# Revit family: Hager-IC-IP30-syst-PL-en
name_source: partatom
category: Electrical Equipment
units: mm (PartAtom-declared; Revit-internal decimal feet)

## family parameters
Cut with Voids When Loaded = No
Host = Face
Panel Configuration = Two Columns, Circuits Across
Part Type = Panelboard
Room Calculation Point = No
Round Connector Dimension = Use Diameter
Shared = No

## types (14) — shared parameters
EF000007 - Colour = EV000202 - White
EF000116 - RAL-number = 9010
EF000118 - With mounting plate = No
EF001062 - EMC-version = No
EF001088 - Extension possible = Yes
EF001131 - Internal depth = 72 mm  [stored 0.23622 ft]
EF001134 - DIN-rail = Yes
EF001596 - Material housing = EV000139 - Plastic
EF004462 - Type of closure = EV000154 - Other
EF005474 - Degree of protection (IP) = EV006410 - IP30
EF006244 - Transparent cover/door = No
EF006306 - With lock = No
EF009212 - Cover model = EV000116 - Closed
EF015941 - Signal passing door = Yes
HG000001 - Number of columns = 1
HG000002 - With door or cover = No
HG000003 - Range = IC
HG000005 - Thickness = 3 mm  [stored 0.00984252 ft]
HG000009 - Double swing door = No
HG000010 - Asymmetric doors = No
HG000011 - Empty rows from bottom = No
HG000017 - Distance between poles = 18 mm  [stored 0.0590551 ft]
Manufacturer = Hager
Type Comments = IC
zero-valued in all types: Default Elevation, HG000007 - Number of empty columns, HG000008 - Number of empty rows

## per-type parameters (varying)
| type | EF000003 - Mounting method | EF000008 - Width | EF000040 - Height | EF000049 - Depth | EF000218 - Built-in depth | EF000266 - Number of rows | EF000332 - Built-in height | EF000846 - Built-in width | EF002950 - Width in number of modular spacings | EF015776 - Earthing terminal block | EF015777 - Neutral terminal block | HG000004 - Manufacturer reference | HG000006 - Flush mounted | Model |
| Recessed mounted IP30 W236 H206 D91.4 8 Modular spacings - VR108NP | EV000383 - Flush mounted (plaster) | 236 mm | 206 mm  [stored 0.675853 ft] | 91 mm  [stored 0.298556 ft] | 72 mm  [stored 0.23622 ft] | 1 | 188 mm  [stored 0.616798 ft] | 218 mm  [stored 0.715223 ft] | 8 | Yes | Yes | VR108NP | Yes | VR108NP |
| Recessed mounted IP30 W308 H226 D91.4 12 Modular spacings - VR112NP | EV000383 - Flush mounted (plaster) | 308 mm  [stored 1.0105 ft] | 226 mm  [stored 0.74147 ft] | 91 mm  [stored 0.298556 ft] | 72 mm  [stored 0.23622 ft] | 1 | 208 mm | 290 mm  [stored 0.951444 ft] | 12 | Yes | Yes | VR112NP | Yes | VR112NP |
| Recessed mounted IP30 W308 H351 D93 12 Modular spacings - VR212NP | EV000383 - Flush mounted (plaster) | 308 mm  [stored 1.0105 ft] | 351 mm  [stored 1.15157 ft] | 93 mm  [stored 0.305118 ft] | 72 mm  [stored 0.23622 ft] | 2 | 333 mm  [stored 1.09252 ft] | 290 mm  [stored 0.951444 ft] | 12 | Yes | Yes | VR212NP | Yes | VR212NP |
| Recessed mounted IP30 W416 H226 D91.4 18 Modular spacings - VR118NP | EV000383 - Flush mounted (plaster) | 416 mm | 226 mm  [stored 0.74147 ft] | 91 mm  [stored 0.298556 ft] | 72 mm  [stored 0.23622 ft] | 1 | 208 mm | 398 mm  [stored 1.30577 ft] | 18 | Yes | Yes | VR118NP | Yes | VR118NP |
| Surface mounted IP30 W134.5 H170 D91 6 Modular spacings - VD106NP | EV000384 - Surface mounted (plaster) | 134 mm | 170 mm  [stored 0.557743 ft] | 91 mm  [stored 0.298556 ft] | 0 mm  [stored 0 ft] | 1 | 0 mm  [stored 0 ft] | 0 mm  [stored 0 ft] | 6 | Yes | Yes | VD106NP | No | VD106NP |
| Surface mounted IP30 W170.5 H170 D91 8 Modular spacings - VD108NP | EV000384 - Surface mounted (plaster) | 170 mm  [stored 0.557743 ft] | 170 mm  [stored 0.557743 ft] | 91 mm  [stored 0.298556 ft] | 0 mm  [stored 0 ft] | 1 | 0 mm  [stored 0 ft] | 0 mm  [stored 0 ft] | 8 | Yes | Yes | VD108NP | No | VD108NP |
| Surface mounted IP30 W206.5 H170 D91 10 Modular spacings - VD110NP | EV000384 - Surface mounted (plaster) | 206 mm  [stored 0.675853 ft] | 170 mm  [stored 0.557743 ft] | 91 mm  [stored 0.298556 ft] | 0 mm  [stored 0 ft] | 1 | 0 mm  [stored 0 ft] | 0 mm  [stored 0 ft] | 10 | Yes | Yes | VD110NP | No | VD110NP |
| Surface mounted IP30 W27.5 H163.5 D71 1 Modular spacings - VD101NE | EV000384 - Surface mounted (plaster) | 28 mm  [stored 0.0918635 ft] | 164 mm  [stored 0.538058 ft] | 71 mm  [stored 0.23294 ft] | 0 mm  [stored 0 ft] | 1 | 0 mm  [stored 0 ft] | 0 mm  [stored 0 ft] | 1 | No | No | VD101NE | No | VD101NE |
| Surface mounted IP30 W292.5 H200 D91 12 Modular spacings - VD112NP | EV000384 - Surface mounted (plaster) | 292 mm  [stored 0.958005 ft] | 200 mm  [stored 0.656168 ft] | 91 mm  [stored 0.298556 ft] | 0 mm  [stored 0 ft] | 1 | 0 mm  [stored 0 ft] | 0 mm  [stored 0 ft] | 12 | Yes | Yes | VD112NP | No | VD112NP |
| Surface mounted IP30 W294 H326.5 D92.5 12 Modular spacings - VD212NP | EV000384 - Surface mounted (plaster) | 294 mm  [stored 0.964567 ft] | 326 mm  [stored 1.06955 ft] | 92 mm  [stored 0.301837 ft] | 0 mm  [stored 0 ft] | 2 | 0 mm  [stored 0 ft] | 0 mm  [stored 0 ft] | 12 | Yes | Yes | VD212NP | No | VD212NP |
| Surface mounted IP30 W400 H200 D91 18 Modular spacings - VD118NP | EV000384 - Surface mounted (plaster) | 400 mm  [stored 1.31234 ft] | 200 mm  [stored 0.656168 ft] | 91 mm  [stored 0.298556 ft] | 0 mm  [stored 0 ft] | 1 | 0 mm  [stored 0 ft] | 0 mm  [stored 0 ft] | 18 | Yes | Yes | VD118NP | No | VD118NP |
| Surface mounted IP30 W45.5 H163.5 D71 2 Modular spacings - VD102NE | EV000384 - Surface mounted (plaster) | 46 mm  [stored 0.150919 ft] | 164 mm  [stored 0.538058 ft] | 71 mm  [stored 0.23294 ft] | 0 mm  [stored 0 ft] | 1 | 0 mm  [stored 0 ft] | 0 mm  [stored 0 ft] | 2 | No | No | VD102NE | No | VD102NE |
| Surface mounted IP30 W63.5 H163.5 D71 3 Modular spacings - VD103NE | EV000384 - Surface mounted (plaster) | 64 mm  [stored 0.209974 ft] | 164 mm  [stored 0.538058 ft] | 71 mm  [stored 0.23294 ft] | 0 mm  [stored 0 ft] | 1 | 0 mm  [stored 0 ft] | 0 mm  [stored 0 ft] | 3 | No | No | VD103NE | No | VD103NE |
| Surface mounted IP30 W81.5 H163.5 D71 4 Modular spacings - VD104NE | EV000384 - Surface mounted (plaster) | 82 mm  [stored 0.269029 ft] | 164 mm  [stored 0.538058 ft] | 71 mm  [stored 0.23294 ft] | 0 mm  [stored 0 ft] | 1 | 0 mm  [stored 0 ft] | 0 mm  [stored 0 ft] | 4 | No | No | VD104NE | No | VD104NE |

note: [stored X ft] marks values corroborated as IEEE doubles in the binary element streams (Revit-internal decimal feet)

## geometry (parser evidence)
native form markers: Sweep x17
no freeform markers — native parametric forms only
